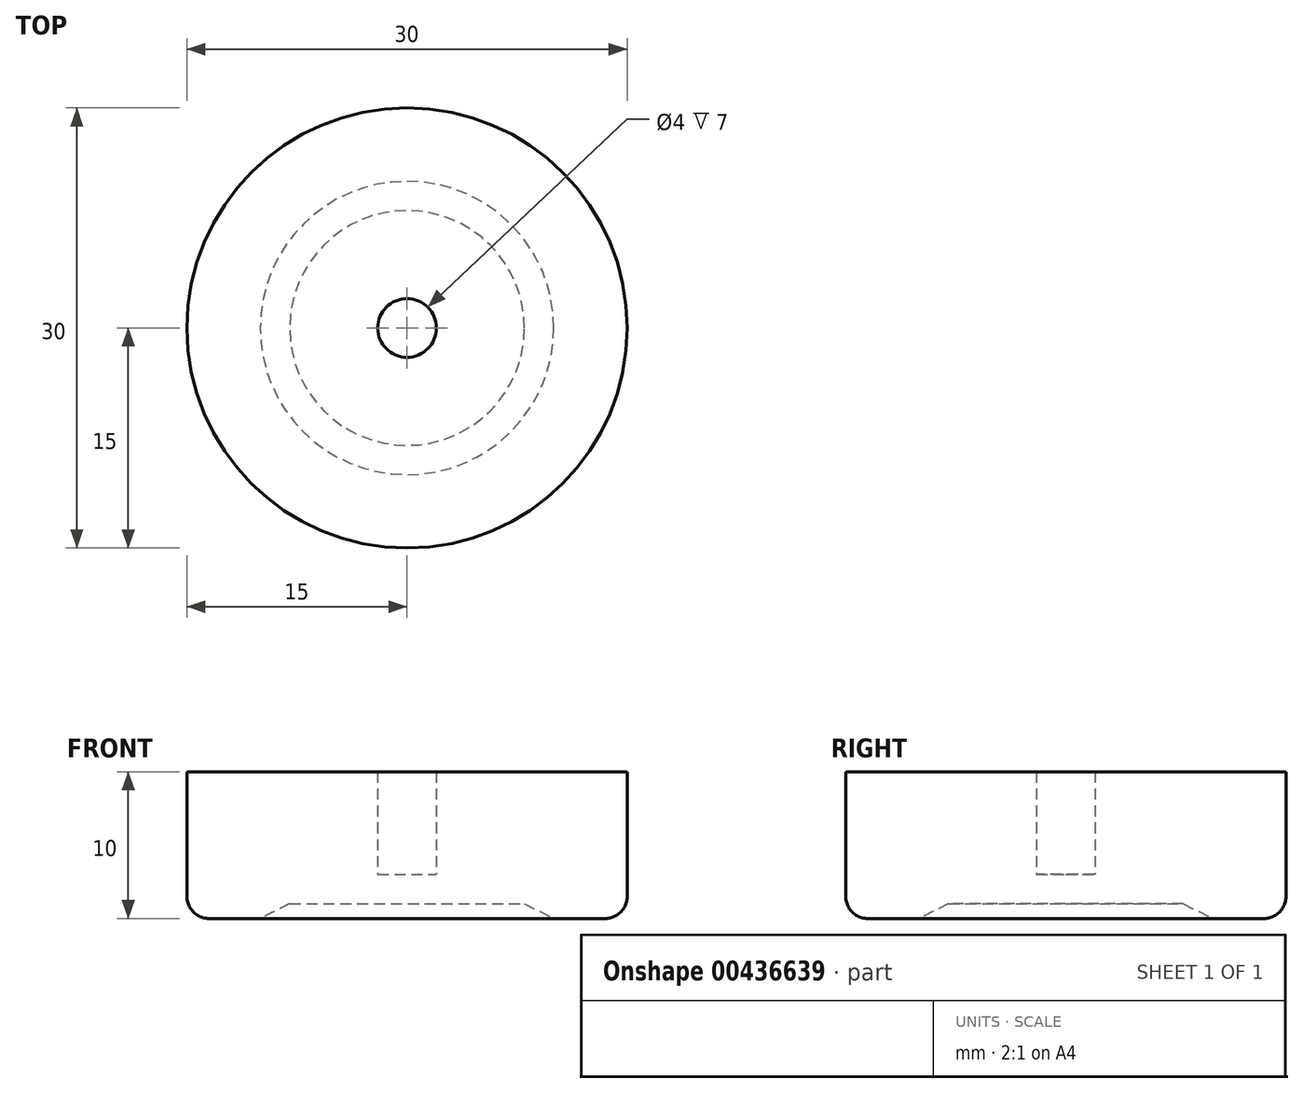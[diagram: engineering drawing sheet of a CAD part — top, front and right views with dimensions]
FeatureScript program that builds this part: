
annotation { "Feature Type Name" : "Feature", "Feature Type Description" : "" }
export const myFeature = defineFeature(function(context is Context, id is Id, definition is map)
    precondition{}
    {
        {
            var Q0;
            Q0=qCreatedBy(makeId("Front.planeOp"),FACE);
            var sketch = newSketch(context, id + "F0", { "sketchPlane" : qUnion([Q0])});
            skLineSegment(sketch, "E0", {"start": v(0, 0) * mm, "end": v(15, 0) * mm});
            skLineSegment(sketch, "E1", {"start": v(15, 0) * mm, "end": v(15, -10) * mm});
            skLineSegment(sketch, "E2", {"start": v(15, -10) * mm, "end": v(10, -10) * mm});
            skLineSegment(sketch, "E3", {"start": v(0, -9) * mm, "end": v(0, 0) * mm});
            skLineSegment(sketch, "E4", {"start": v(0, -9) * mm, "end": v(8, -9) * mm});
            skLineSegment(sketch, "E5", {"start": v(8, -9) * mm, "end": v(10, -10) * mm});
            skLineSegment(sketch, "E6", {"start": v(2, 0) * mm, "end": v(2, -7) * mm});
            skLineSegment(sketch, "E7", {"start": v(2, -7) * mm, "end": v(0, -7) * mm});
            skSolve(sketch);
        }
        {
            var Q0;
            {var subQ3=sQuery(id+"F0.wireOp",EDGE,"E1");Q0=makeQuery(id+"F0.imprint","IMPRINT",FACE,{"disambiguationData":[TD([[makeQuery(id+"F0.imprint","IMPRINT",EDGE,{"derivedFrom":subQ3}),-1.0]])]});}
            var Q1;
            Q1=sQuery(id+"F0.wireOp",EDGE,"E3");
            revolve(context, id + "F1", {"entities" : qUnion([Q0]), "axis" : qUnion([Q1]), "revolveType" : RevolveType.FULL});
        }
        {
            var Q0;
            Q0=makeQuery(id+"F1.opRevolve","SWEPT_EDGE",EDGE,{"disambiguationData":[OSD([sQuery(id+"F0.wireOp",EDGE,"E1"),sQuery(id+"F0.wireOp",EDGE,"E2")])]});
            fillet(context, id + "F2", {"entities" : qUnion([Q0]), "radius" : 1.5 * mm, "tangentPropagation" : true, "allowEdgeOverflow" : false});
        }
    });
